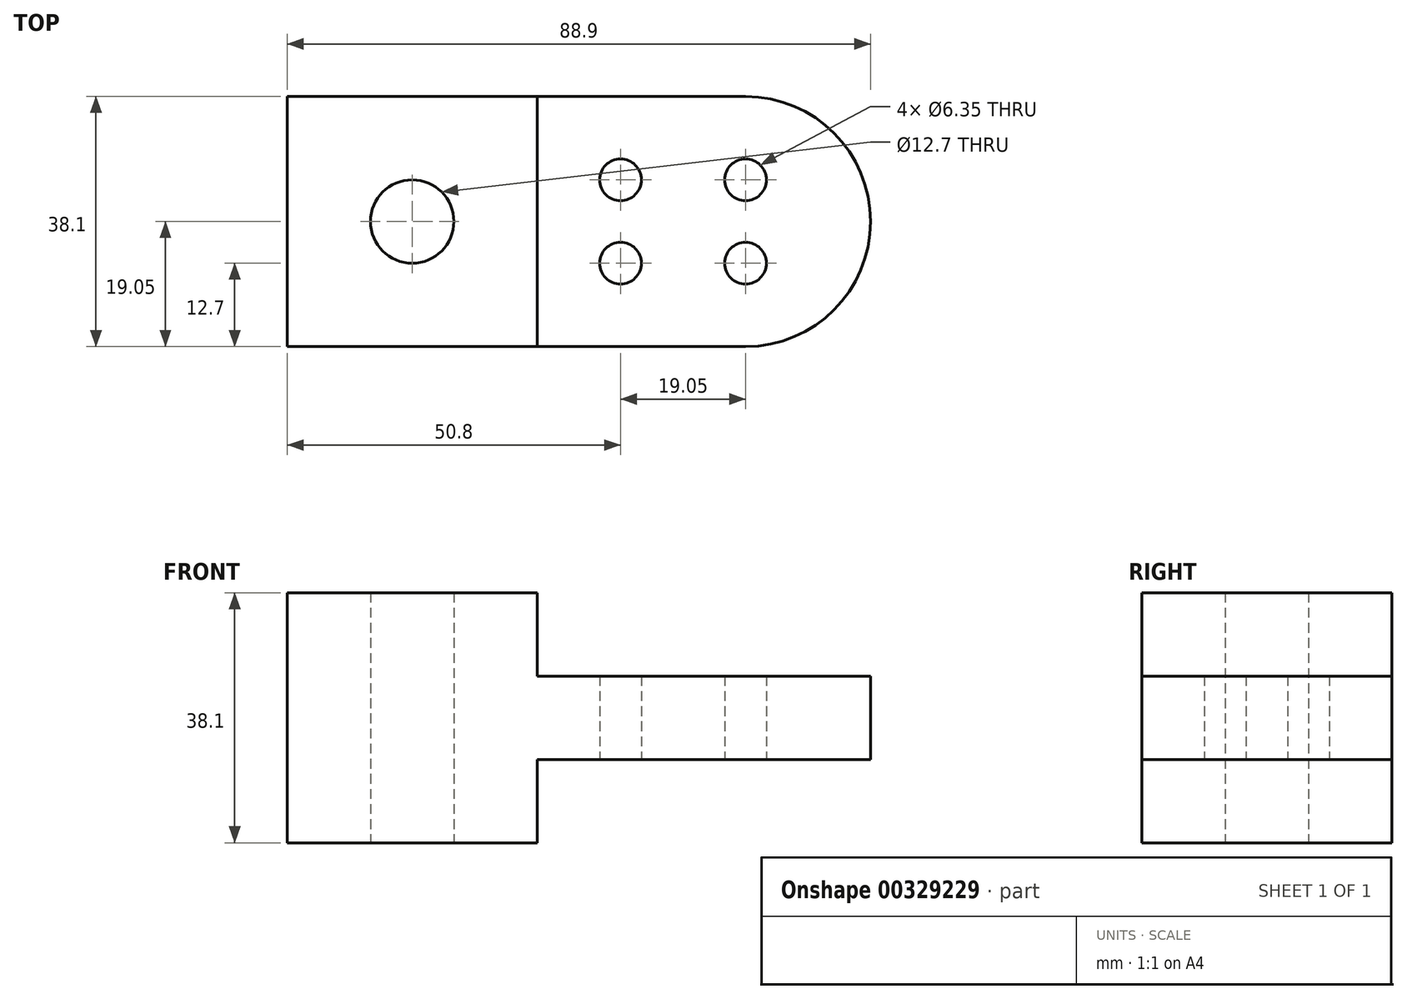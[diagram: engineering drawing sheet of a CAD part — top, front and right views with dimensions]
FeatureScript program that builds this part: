
annotation { "Feature Type Name" : "Feature", "Feature Type Description" : "" }
export const myFeature = defineFeature(function(context is Context, id is Id, definition is map)
    precondition{}
    {
        {
            var Q0;
            Q0=qCreatedBy(makeId("Top.planeOp"),FACE);
            var sketch = newSketch(context, id + "F0", { "sketchPlane" : qUnion([Q0])});
            skLineSegment(sketch, "E0", {"start": v(0, 0) * mm, "end": v(0, 38.1) * mm});
            skLineSegment(sketch, "E1", {"start": v(0, 38.1) * mm, "end": v(38.1, 38.1) * mm});
            skLineSegment(sketch, "E2", {"start": v(38.1, 38.1) * mm, "end": v(38.1, 0) * mm});
            skLineSegment(sketch, "E3", {"start": v(38.1, 0) * mm, "end": v(0, 0) * mm});
            skLineSegment(sketch, "E4", {"start": v(38.1, 0) * mm, "end": v(69.85, 0) * mm});
            skLineSegment(sketch, "E5", {"start": v(38.1, 38.1) * mm, "end": v(69.85, 38.1) * mm});
            skArc(sketch, "E6", {"start": v(69.85, 38.1) * mm, "mid": v(88.9, 19.05) * mm, "end": v(69.85, 0) * mm});
            skLineSegment(sketch, "E7.bottom", {"start": v(50.8, 25.4) * mm, "end": v(69.85, 25.4) * mm, "construction": true});
            skLineSegment(sketch, "E7.top", {"start": v(50.8, 12.7) * mm, "end": v(69.85, 12.7) * mm, "construction": true});
            skLineSegment(sketch, "E7.left", {"start": v(50.8, 25.4) * mm, "end": v(50.8, 12.7) * mm, "construction": true});
            skLineSegment(sketch, "E7.right", {"start": v(69.85, 25.4) * mm, "end": v(69.85, 12.7) * mm, "construction": true});
            skCircle(sketch, "E8", {"center": v(50.8, 25.4) * mm, "radius": 3.18 * mm});
            skCircle(sketch, "E9", {"center": v(69.85, 25.4) * mm, "radius": 3.18 * mm});
            skCircle(sketch, "E10", {"center": v(50.8, 12.7) * mm, "radius": 3.18 * mm});
            skCircle(sketch, "E11", {"center": v(69.85, 12.7) * mm, "radius": 3.18 * mm});
            skCircle(sketch, "E12", {"center": v(19.05, 19.05) * mm, "radius": 6.35 * mm});
            skSolve(sketch);
        }
        {
            var Q0;
            Q0=makeQuery(id+"F0.imprint","IMPRINT",FACE,{"disambiguationData":[TD([[makeQuery(id+"F0.imprint","IMPRINT",EDGE,{"derivedFrom":sQuery(id+"F0.wireOp",EDGE,"E0")}),-1.0]])]});
            extrude(context, id + "F1", {"entities" : qUnion([Q0]), "endBound" : BoundingType.SYMMETRIC, "depth" : 38.1 * mm});
        }
        {
            var Q0;
            Q0=makeQuery(id+"F0.imprint","IMPRINT",FACE,{"disambiguationData":[TD([[makeQuery(id+"F0.imprint","IMPRINT",EDGE,{"derivedFrom":sQuery(id+"F0.wireOp",EDGE,"E2")}),1.0]])]});
            extrude(context, id + "F2", {"entities" : qUnion([Q0]), "operationType" : NewBodyOperationType.ADD, "endBound" : BoundingType.SYMMETRIC, "depth" : 12.7 * mm});
        }
    });
